# Revit family: 304_A____Y_B_E
name_source: partatom
category: Pipe Accessories
units: mm (PartAtom-declared; Revit-internal decimal feet)

## family parameters
Always vertical = Yes
Cut with Voids When Loaded = No
Part Type = Valve - Breaks Into
Round Connector Dimension = Use Diameter
Shared = No
Work Plane-Based = No

## types (3) — shared parameters
Description = E-Just - Dynamic Balancing valve - Adjusteble Cartridge
L2D_Min = 3048 mm  [stored 10 ft]
L4 = 11 mm  [stored 0.0360892 ft]
L5 = 18 mm  [stored 0.0590551 ft]
LA = 31 mm  [stored 0.101706 ft]
Manufacturer = FlowCon
QmdConnectorList = 301;D;302;D
RA = 11 mm  [stored 0.0360892 ft]
URL = http://flowcon.com
magiPartTypeId = 304
magiProductFamilyId = A*.*.Y.B.E
zero-valued in all types: MC_Default_elevation

## per-type parameters (varying)
| type | CenSd_RN_6 | CenSd_SW_6 | D | H11 | H12 | L1 | L1__ve | L2 | L2D | L6 | L6__ve | LL | R1 | R2 | R3 | RN | SW | W2D |
| A15.I.Y.B.E | 9 mm | 12 mm  [stored 0.0393701 ft] | 15 mm | 25 mm  [stored 0.082021 ft] | 32 mm | 16 mm  [stored 0.0524934 ft] | -16 mm  [stored -0.0524934 ft] | 48 mm  [stored 0.15748 ft] | 80 mm | 37 mm | -37 mm | 40 mm  [stored 0.131234 ft] | 11 mm  [stored 0.0360892 ft] | 13 mm | 14 mm  [stored 0.0459318 ft] | 10 mm  [stored 0.0328084 ft] | 14 mm  [stored 0.0459318 ft] | 15 mm  [stored 0.0492126 ft] |
| A25.I.K.Y.B.E | 11 mm  [stored 0.0360892 ft] | 16 mm  [stored 0.0524934 ft] | 25 mm | 23 mm | 31 mm  [stored 0.101706 ft] | 18 mm  [stored 0.0590551 ft] | -18 mm | 55 mm | 91 mm | 36 mm | -36 mm | 46 mm | 14 mm  [stored 0.0459318 ft] | 16 mm  [stored 0.0524934 ft] | 18 mm  [stored 0.0590551 ft] | 13 mm | 18 mm  [stored 0.0590551 ft] | 25 mm  [stored 0.082021 ft] |
| A20.I.Y.B.E | 10 mm  [stored 0.0328084 ft] | 14 mm  [stored 0.0459318 ft] | 20 mm | 24 mm  [stored 0.0787402 ft] | 31 mm  [stored 0.101706 ft] | 16 mm  [stored 0.0524934 ft] | -16 mm  [stored -0.0524934 ft] | 48 mm  [stored 0.15748 ft] | 80 mm | 36 mm | -36 mm | 40 mm  [stored 0.131234 ft] | 12 mm  [stored 0.0393701 ft] | 14 mm  [stored 0.0459318 ft] | 16 mm  [stored 0.0524934 ft] | 12 mm  [stored 0.0393701 ft] | 16 mm  [stored 0.0524934 ft] | 20 mm  [stored 0.0656168 ft] |

note: column(s) folded — value = type name in every type: magiProductCode, magiProductId

note: [stored X ft] marks values corroborated as IEEE doubles in the binary element streams (Revit-internal decimal feet)

## geometry (parser evidence)
native form markers: Sweep x2
no freeform markers — native parametric forms only
